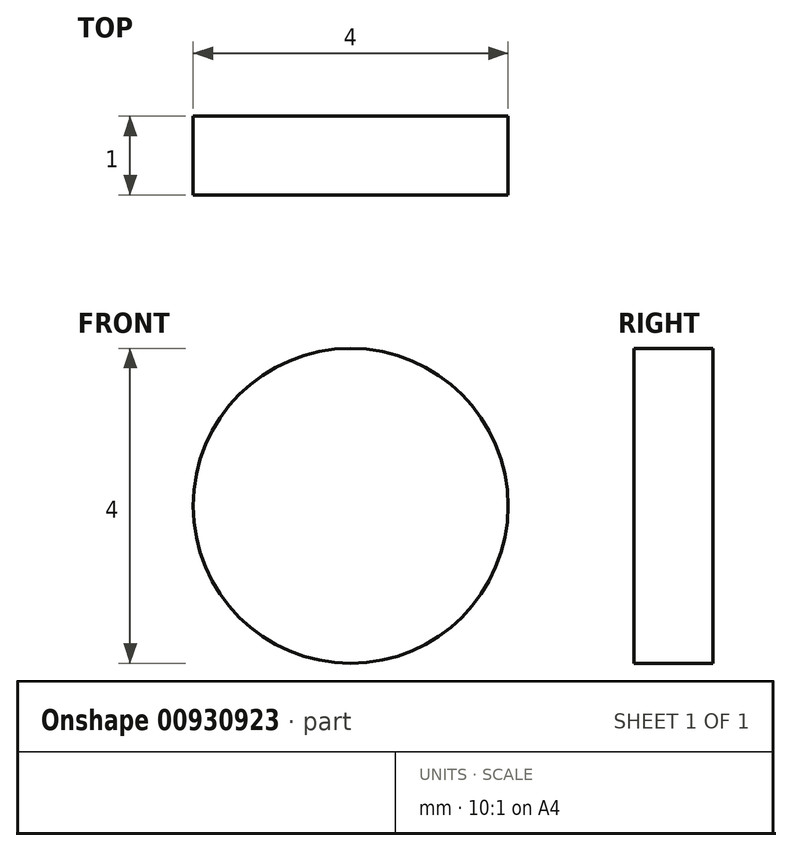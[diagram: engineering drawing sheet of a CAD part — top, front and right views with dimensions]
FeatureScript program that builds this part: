
annotation { "Feature Type Name" : "Feature", "Feature Type Description" : "" }
export const myFeature = defineFeature(function(context is Context, id is Id, definition is map)
    precondition{}
    {
        {
            var Q0;
            Q0=qCreatedBy(makeId("Front.planeOp"),FACE);
            var sketch = newSketch(context, id + "F0", { "sketchPlane" : qUnion([Q0])});
            skCircle(sketch, "E0", {"center": v(0, 0) * mm, "radius": 2 * mm});
            skSolve(sketch);
        }
        {
            var Q0;
            Q0=makeQuery(id+"F0.imprint","IMPRINT",FACE,{"disambiguationData":[TD([[makeQuery(id+"F0.imprint","IMPRINT",EDGE,{"derivedFrom":sQuery(id+"F0.wireOp",EDGE,"E0")}),1.0]])]});
            extrude(context, id + "F1", {"entities" : qUnion([Q0]), "depth" : 1 * mm, "offsetDistance" : 25 * mm});
        }
    });
